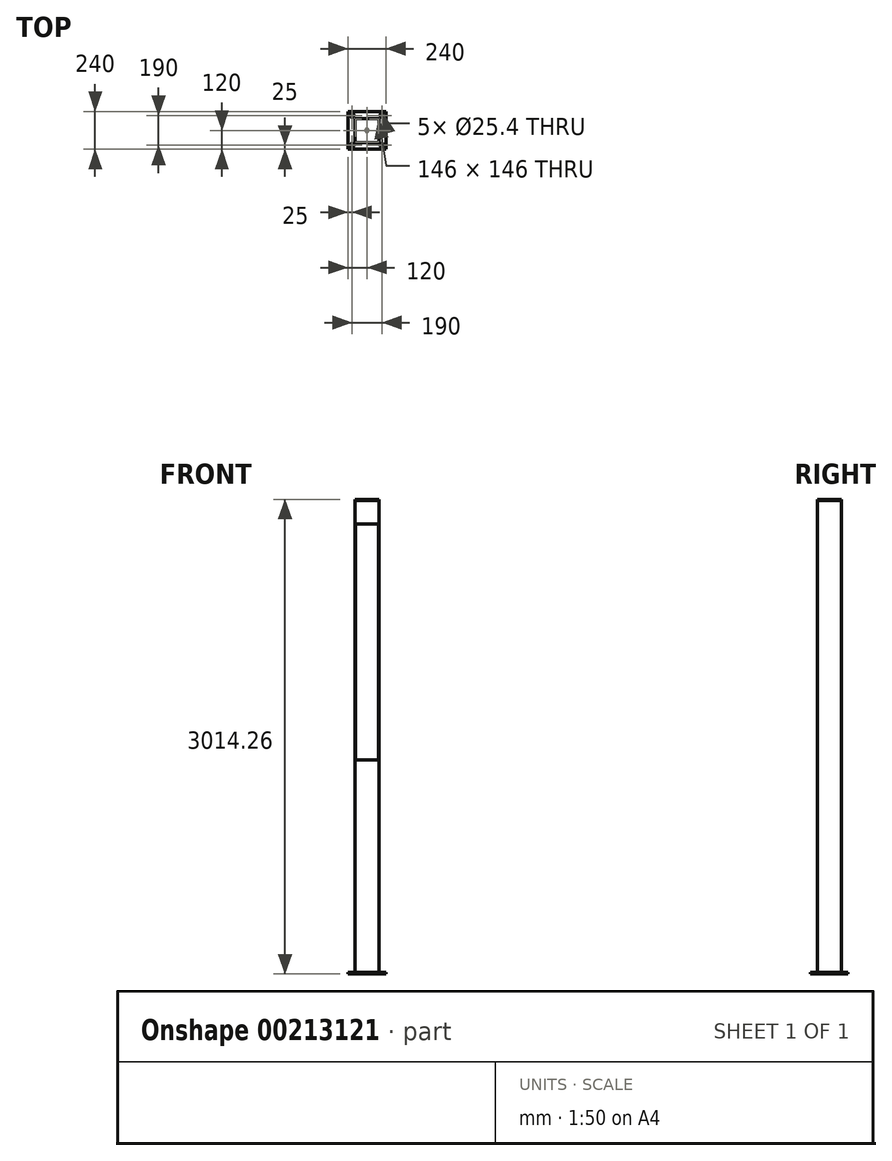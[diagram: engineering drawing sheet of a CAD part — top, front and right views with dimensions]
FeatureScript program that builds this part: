
annotation { "Feature Type Name" : "Feature", "Feature Type Description" : "" }
export const myFeature = defineFeature(function(context is Context, id is Id, definition is map)
    precondition{}
    {
        {
            var Q0;
            Q0=qCreatedBy(makeId("Top.planeOp"),FACE);
            var sketch = newSketch(context, id + "F0", { "sketchPlane" : qUnion([Q0])});
            skLineSegment(sketch, "E0.bottom", {"start": v(76.2, 76.2) * mm, "end": v(-76.2, 76.2) * mm});
            skLineSegment(sketch, "E0.top", {"start": v(76.2, -76.2) * mm, "end": v(-76.2, -76.2) * mm});
            skLineSegment(sketch, "E0.left", {"start": v(76.2, 76.2) * mm, "end": v(76.2, -76.2) * mm});
            skLineSegment(sketch, "E0.right", {"start": v(-76.2, 76.2) * mm, "end": v(-76.2, -76.2) * mm});
            skPoint(sketch, "E0.middle", {"position": v(0, 0) * mm});
            skLineSegment(sketch, "E1.0", {"start": v(73, 73) * mm, "end": v(-73, 73) * mm});
            skLineSegment(sketch, "E1.1", {"start": v(73, 73) * mm, "end": v(73, -73) * mm});
            skLineSegment(sketch, "E1.2", {"start": v(73, -73) * mm, "end": v(-73, -73) * mm});
            skLineSegment(sketch, "E1.3", {"start": v(-73, 73) * mm, "end": v(-73, -73) * mm});
            skSolve(sketch);
        }
        {
            var Q0;
            Q0 = qSketchRegion(id + "F0", true);
            extrude(context, id + "F1", {"entities" : qUnion([Q0]), "depth" : 3000 * mm});
        }
        {
            var Q0;
            Q0=makeQuery(id+"F1.opExtrude","SWEPT_FACE",FACE,{"disambiguationData":[OSD([sQuery(id+"F0.wireOp",EDGE,"E0.top")])]});
            var sketch = newSketch(context, id + "F2", { "sketchPlane" : qUnion([Q0])});
            skLineSegment(sketch, "E2", {"start": v(0, 3000) * mm, "end": v(0, 2850) * mm, "construction": true});
            skPoint(sketch, "E2.endSnap0", {"position": v(0, 3000) * mm});
            skLineSegment(sketch, "E3", {"start": v(0, 2850) * mm, "end": v(73, 2850) * mm, "construction": true});
            skLineSegment(sketch, "E4", {"start": v(0, 2850) * mm, "end": v(-73, 2850) * mm, "construction": true});
            skLineSegment(sketch, "E5", {"start": v(-73, 2850) * mm, "end": v(-73, 1350) * mm});
            skLineSegment(sketch, "E6", {"start": v(-73, 1350) * mm, "end": v(73, 1350) * mm});
            skLineSegment(sketch, "E7", {"start": v(73, 2850) * mm, "end": v(73, 1350) * mm});
            skLineSegment(sketch, "E8", {"start": v(-73, 2850) * mm, "end": v(73, 2850) * mm});
            skSolve(sketch);
        }
        {
            var Q0;
            Q0 = qSketchRegion(id + "F2", true);
            extrude(context, id + "F3", {"entities" : qUnion([Q0]), "operationType" : NewBodyOperationType.REMOVE, "oppositeDirection" : true, "depth" : 152.4 * mm - 3.6 * mm});
        }
        {
            var Q0;
            Q0=qCreatedBy(makeId("Right.planeOp"),FACE);
            var sketch = newSketch(context, id + "F4", { "sketchPlane" : qUnion([Q0])});
            skLineSegment(sketch, "E9", {"start": v(32.6, 3007.26) * mm, "end": v(32.6, 2837.26) * mm, "construction": true});
            skLineSegment(sketch, "E10", {"start": v(-71.22, 1344.85) * mm, "end": v(32.6, 2837.26) * mm, "construction": true});
            skLineSegment(sketch, "E11.0", {"start": v(-70.82, 1316.36) * mm, "end": v(36.3, 2856.02) * mm});
            skLineSegment(sketch, "E12.0", {"start": v(-75.55, 1317) * mm, "end": v(31.56, 2856.64) * mm});
            skLineSegment(sketch, "E13", {"start": v(-75.55, 1317) * mm, "end": v(-70.82, 1316.36) * mm});
            skLineSegment(sketch, "E14", {"start": v(31.56, 2856.64) * mm, "end": v(36.3, 2856.02) * mm});
            skSolve(sketch);
        }
        {
            var Q0;
            Q0=sQuery(id+"F4.wireOp",EDGE,"E12.0");
            extrude(context, id + "F5", {"bodyType" : ToolBodyType.SURFACE, "surfaceEntities" : qUnion([Q0]), "endBound" : BoundingType.SYMMETRIC, "depth" : 152.4 * mm - 3.2 * mm - 3.2 * mm});
        }
        {
            var Q0;
            Q0=makeQuery(id+"F1.opExtrude","CAP_FACE",FACE,{"disambiguationData":[OSD([sQuery(id+"F0.wireOp",EDGE,"E0.bottom"),sQuery(id+"F0.wireOp",EDGE,"E0.top"),sQuery(id+"F0.wireOp",EDGE,"E0.left"),sQuery(id+"F0.wireOp",EDGE,"E0.right"),sQuery(id+"F0.wireOp",EDGE,"E1.0"),sQuery(id+"F0.wireOp",EDGE,"E1.1"),sQuery(id+"F0.wireOp",EDGE,"E1.2"),sQuery(id+"F0.wireOp",EDGE,"E1.3")])],"isStart":false});
            var sketch = newSketch(context, id + "F6", { "sketchPlane" : qUnion([Q0])});
            skLineSegment(sketch, "E15.bottom", {"start": v(-76.2, 76.2) * mm, "end": v(76.2, 76.2) * mm});
            skLineSegment(sketch, "E15.top", {"start": v(-76.2, -76.2) * mm, "end": v(76.2, -76.2) * mm});
            skLineSegment(sketch, "E15.left", {"start": v(-76.2, 76.2) * mm, "end": v(-76.2, -76.2) * mm});
            skLineSegment(sketch, "E15.right", {"start": v(76.2, 76.2) * mm, "end": v(76.2, -76.2) * mm});
            skLineSegment(sketch, "E16.bottom", {"start": v(73, -73) * mm, "end": v(-73, -73) * mm, "construction": true});
            skLineSegment(sketch, "E16.top", {"start": v(73, 73) * mm, "end": v(-73, 73) * mm, "construction": true});
            skLineSegment(sketch, "E16.left", {"start": v(73, -73) * mm, "end": v(73, 73) * mm, "construction": true});
            skLineSegment(sketch, "E16.right", {"start": v(-73, -73) * mm, "end": v(-73, 73) * mm, "construction": true});
            skSolve(sketch);
        }
        {
            var Q0;
            Q0=makeQuery(id+"F6.imprint","IMPRINT",FACE,{"disambiguationData":[TD([[makeQuery(id+"F6.imprint","IMPRINT",EDGE,{"derivedFrom":sQuery(id+"F6.wireOp",EDGE,"E15.bottom")}),1.0]])]});
            var Q1;
            Q1=makeQuery(id+"F6.imprint","IMPRINT",FACE,{"disambiguationData":[TD([[makeQuery(id+"F6.imprint","IMPRINT",EDGE,{"derivedFrom":makeQuery(id+"F1.opExtrude","CAP_EDGE",EDGE,{"disambiguationData":[OSD([sQuery(id+"F0.wireOp",EDGE,"E1.0")])],"isStart":false})}),1.0]])]});
            var Q2;
            Q2=sQuery(id+"F6.wireOp",EDGE,"E16.top");
            var Q3;
            Q3=sQuery(id+"F6.wireOp",EDGE,"E16.left");
            var Q4;
            Q4=sQuery(id+"F6.wireOp",EDGE,"E16.bottom");
            extrude(context, id + "F7", {"entities" : qUnion([Q0, Q1]), "surfaceEntities" : qUnion([Q2, Q3, Q4]), "depth" : 4.76 * mm});
        }
        {
            var Q0;
            Q0=makeQuery(id+"F1.opExtrude","CAP_FACE",FACE,{"disambiguationData":[OSD([sQuery(id+"F0.wireOp",EDGE,"E0.bottom"),sQuery(id+"F0.wireOp",EDGE,"E0.top"),sQuery(id+"F0.wireOp",EDGE,"E0.left"),sQuery(id+"F0.wireOp",EDGE,"E0.right"),sQuery(id+"F0.wireOp",EDGE,"E1.0"),sQuery(id+"F0.wireOp",EDGE,"E1.1"),sQuery(id+"F0.wireOp",EDGE,"E1.2"),sQuery(id+"F0.wireOp",EDGE,"E1.3")])],"isStart":true});
            var sketch = newSketch(context, id + "F8", { "sketchPlane" : qUnion([Q0])});
            skLineSegment(sketch, "E17.bottom", {"start": v(-120, 120) * mm, "end": v(120, 120) * mm});
            skLineSegment(sketch, "E17.top", {"start": v(-120, -120) * mm, "end": v(120, -120) * mm});
            skLineSegment(sketch, "E17.left", {"start": v(-120, 120) * mm, "end": v(-120, -120) * mm});
            skLineSegment(sketch, "E17.right", {"start": v(120, 120) * mm, "end": v(120, -120) * mm});
            skPoint(sketch, "E17.middle", {"position": v(0, 0) * mm});
            skSolve(sketch);
        }
        {
            var Q0;
            Q0 = qSketchRegion(id + "F8", true);
            extrude(context, id + "F9", {"entities" : qUnion([Q0]), "depth" : 9.5 * mm});
        }
        {
            var Q0;
            Q0=makeQuery(id+"F9.opExtrude","CAP_FACE",FACE,{"disambiguationData":[OSD([sQuery(id+"F8.wireOp",EDGE,"E17.bottom"),sQuery(id+"F8.wireOp",EDGE,"E17.top"),sQuery(id+"F8.wireOp",EDGE,"E17.left"),sQuery(id+"F8.wireOp",EDGE,"E17.right")])],"isStart":false});
            var sketch = newSketch(context, id + "F10", { "sketchPlane" : qUnion([Q0])});
            skLineSegment(sketch, "E18.bottom", {"start": v(-95, 95) * mm, "end": v(95, 95) * mm, "construction": true});
            skLineSegment(sketch, "E18.top", {"start": v(-95, -95) * mm, "end": v(95, -95) * mm, "construction": true});
            skLineSegment(sketch, "E18.left", {"start": v(-95, 95) * mm, "end": v(-95, -95) * mm, "construction": true});
            skLineSegment(sketch, "E18.right", {"start": v(95, 95) * mm, "end": v(95, -95) * mm, "construction": true});
            skPoint(sketch, "E18.middle", {"position": v(0, 0) * mm});
            skCircle(sketch, "E19", {"center": v(-95, 95) * mm, "radius": 12.7 * mm});
            skCircle(sketch, "E20.MirrorC", {"center": v(-95, -95) * mm, "radius": 12.7 * mm});
            skCircle(sketch, "E21.MirrorC", {"center": v(95, 95) * mm, "radius": 12.7 * mm});
            skCircle(sketch, "E22.MirrorC", {"center": v(95, -95) * mm, "radius": 12.7 * mm});
            skCircle(sketch, "E23", {"center": v(0, 0) * mm, "radius": 12.7 * mm});
            skSolve(sketch);
        }
        {
            var Q0;
            Q0 = qSketchRegion(id + "F10", true);
            extrude(context, id + "F11", {"entities" : qUnion([Q0]), "operationType" : NewBodyOperationType.REMOVE, "endBound" : BoundingType.UP_TO_NEXT, "oppositeDirection" : true, "depth" : 25 * mm});
        }
    });
